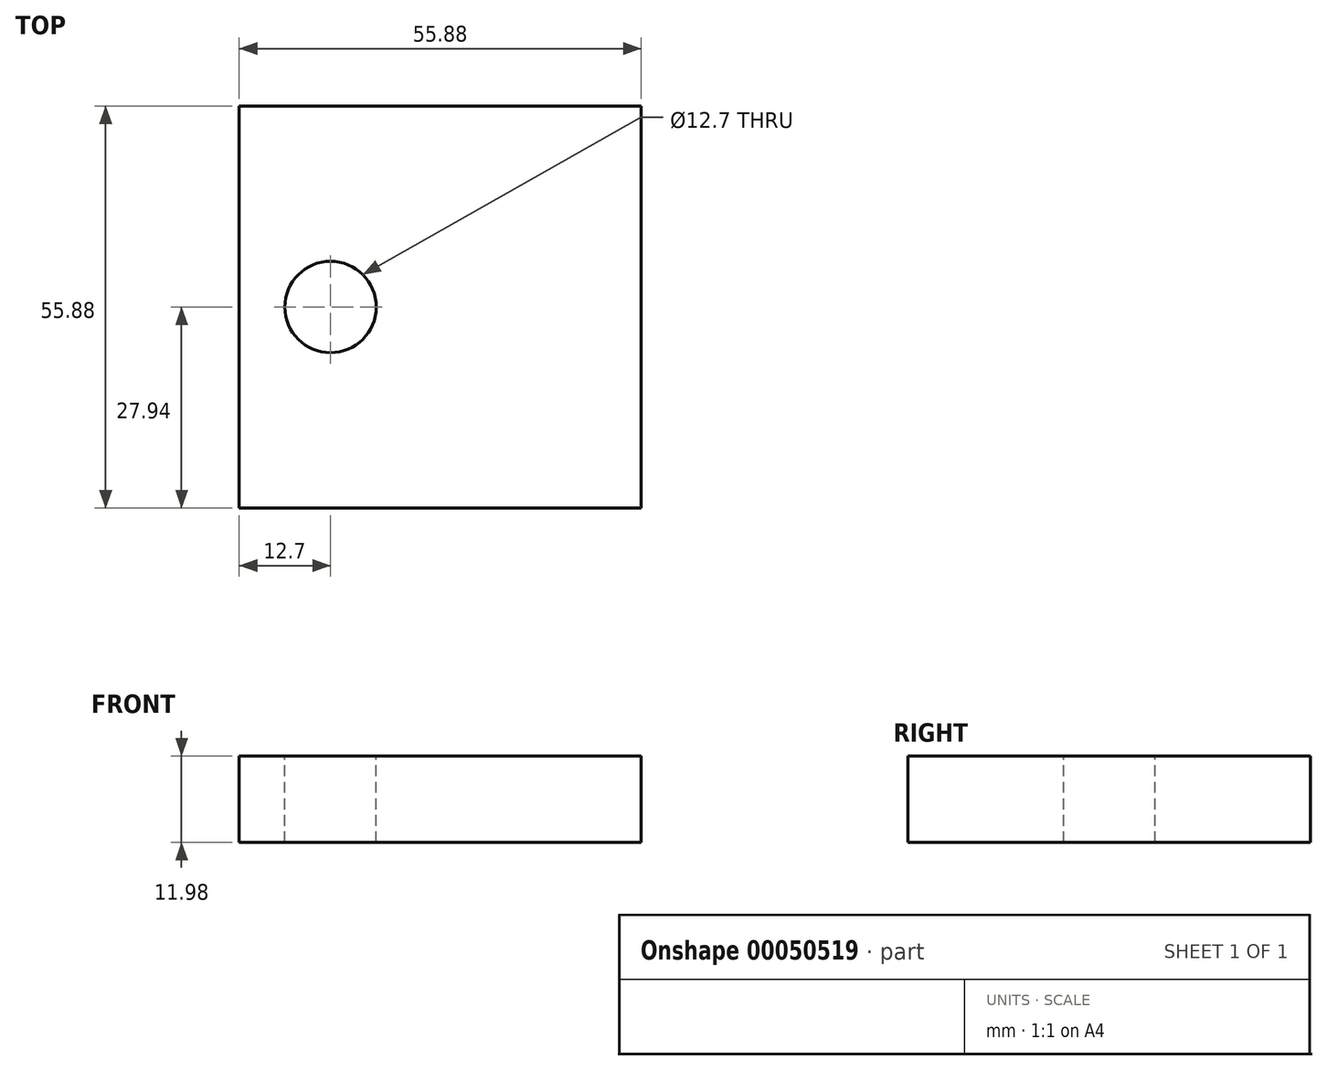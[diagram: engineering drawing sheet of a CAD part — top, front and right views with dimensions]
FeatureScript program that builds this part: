
annotation { "Feature Type Name" : "Feature", "Feature Type Description" : "" }
export const myFeature = defineFeature(function(context is Context, id is Id, definition is map)
    precondition{}
    {
        {
            var Q0;
            Q0=qCreatedBy(makeId("Top.planeOp"),FACE);
            var sketch = newSketch(context, id + "F0", { "sketchPlane" : qUnion([Q0])});
            skLineSegment(sketch, "E0.rect.bottom", {"start": v(27.94, 27.94) * mm, "end": v(-27.94, 27.94) * mm});
            skLineSegment(sketch, "E0.rect.top", {"start": v(27.94, -27.94) * mm, "end": v(-27.94, -27.94) * mm});
            skLineSegment(sketch, "E0.rect.left", {"start": v(27.94, 27.94) * mm, "end": v(27.94, -27.94) * mm});
            skLineSegment(sketch, "E0.rect.right", {"start": v(-27.94, 27.94) * mm, "end": v(-27.94, -27.94) * mm});
            skPoint(sketch, "E0.rect.middle", {"position": v(0, 0) * mm});
            skSolve(sketch);
        }
        {
            var Q0;
            Q0 = qSketchRegion(id + "F0", true);
            extrude(context, id + "F1", {"entities" : qUnion([Q0]), "endBound" : BoundingType.SYMMETRIC, "depth" : 12 * mm});
        }
        {
            var Q0;
            Q0=makeQuery(id+"F1.opExtrude","CAP_FACE",FACE,{"disambiguationData":[OSD([sQuery(id+"F0.wireOp",EDGE,"E0.rect.bottom"),sQuery(id+"F0.wireOp",EDGE,"E0.rect.top"),sQuery(id+"F0.wireOp",EDGE,"E0.rect.left"),sQuery(id+"F0.wireOp",EDGE,"E0.rect.right")])],"isStart":false});
            var sketch = newSketch(context, id + "F2", { "sketchPlane" : qUnion([Q0])});
            skCircle(sketch, "E1", {"center": v(-15.24, 0) * mm, "radius": 6.35 * mm});
            skSolve(sketch);
        }
        {
            var Q0;
            Q0 = qSketchRegion(id + "F2", true);
            extrude(context, id + "F3", {"entities" : qUnion([Q0]), "operationType" : NewBodyOperationType.REMOVE, "endBound" : BoundingType.UP_TO_NEXT, "oppositeDirection" : true, "depth" : 25.4 * mm});
        }
    });
